# Revit family: Screen-Teknion-ZNFGH_Hinged_Screen-R2019
name_source: partatom
category: Furniture
units: mm (PartAtom-declared; Revit-internal decimal feet)

## family parameters
Always vertical = Yes
Cut with Voids When Loaded = No
OmniClass Number = 23.40.20.00
OmniClass Title = General Furniture and Specialties
Room Calculation Point = No
Shared = Yes
Work Plane-Based = No

## types (4) — shared parameters
Assembly Code = E2020200
Manufacturer = Teknion
Manufacturer Fax = 416.661.4586
Part Number = ZNFGH
Product Documentation Link = https://www.teknion.com
Product Line = Zones
Product Page URL = https://www.teknion.com
Series = Screens
Sustainability Data = https://www.teknion.com
URL = www.teknion.com
Unit Weight URL = http://www.teknion.com
Warranty = http://www.teknion.com

## per-type parameters (varying)
| type | Available Angle | Default Elevation | Description | Model | Partial Slot Screen 1 | Partial Slot Screen 2 |
| No Slot Screen 1, No Slot Screen 2 |  | 29.368 " | No Slot Screen 1, No Slot Screen 2 | ZNFGH55NN____ | No | No |
| Partial Slot Screen 1, No Slot Screen 2 |  | 29.368 " | Partial Slot Screen 1, No Slot Screen 2 | ZNFGH55PN____ | Yes | No |
| No Slot Screen 1, Partial Slot Screen 2 |  | 29.368 " | No Slot Screen 1, Partial Slot Screen 2 | ZNFGH55NP____ | No | Yes |
| Partial Slot Screen 1, Partial Slot Screen 2 | The hinged screen can be freely angled between 90°-120° | 17.4 " | Partial Slot Screen1, Partial Slot Screen 2 | ZNFGH55PP____ | Yes | Yes |

## geometry (parser evidence)
native form markers: Sweep x8
no freeform markers — native parametric forms only
